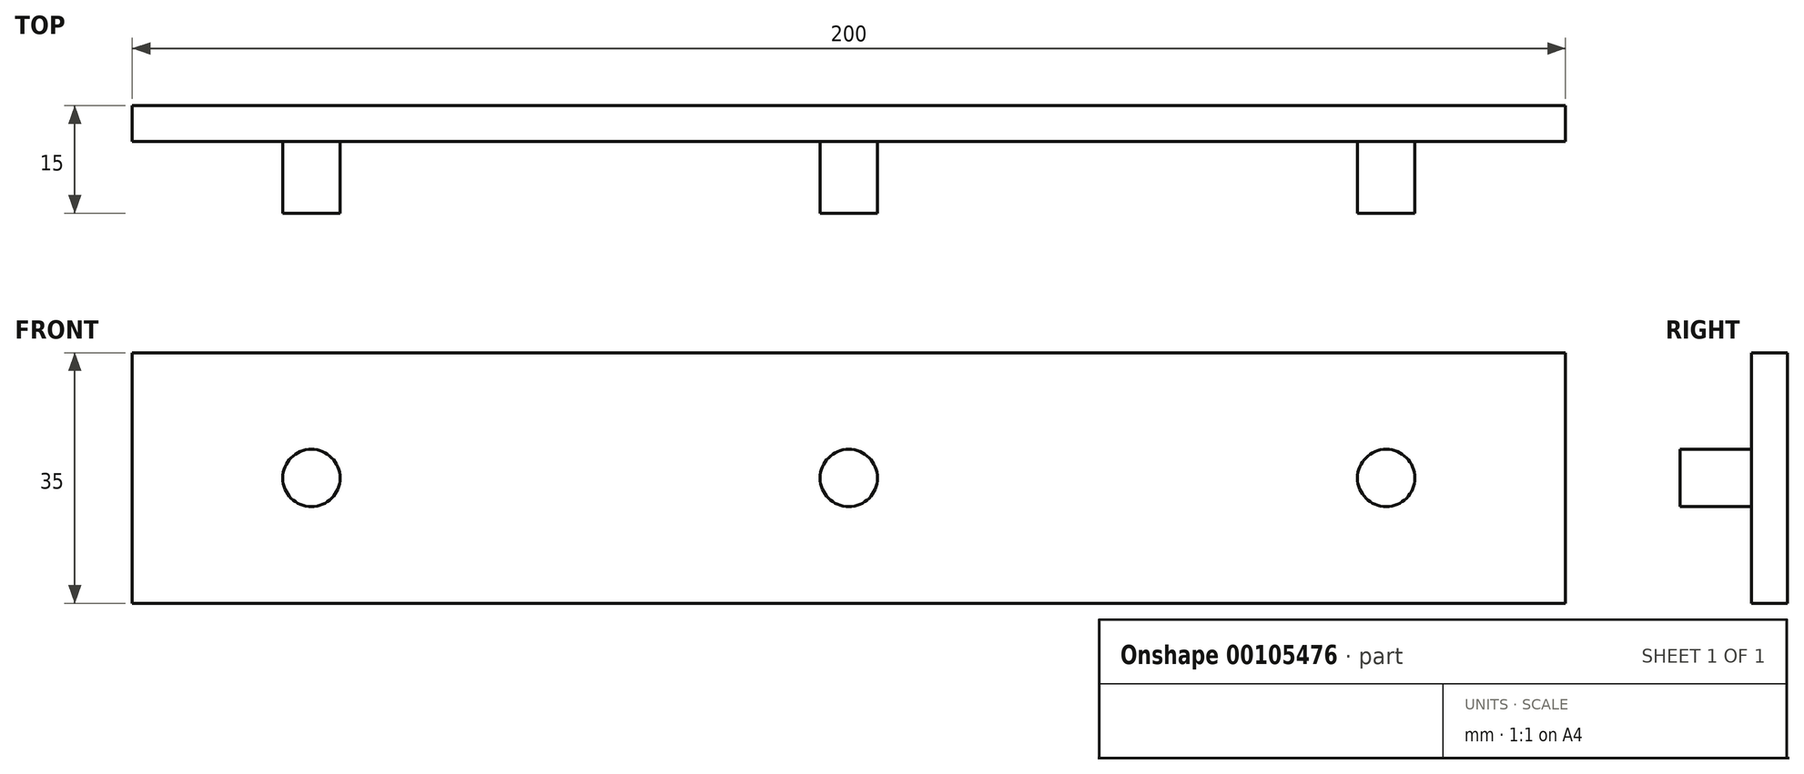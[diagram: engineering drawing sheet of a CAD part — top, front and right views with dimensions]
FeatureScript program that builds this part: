
annotation { "Feature Type Name" : "Feature", "Feature Type Description" : "" }
export const myFeature = defineFeature(function(context is Context, id is Id, definition is map)
    precondition{}
    {
        {
            var Q0;
            Q0=qCreatedBy(makeId("Front.planeOp"),FACE);
            var sketch = newSketch(context, id + "F0", { "sketchPlane" : qUnion([Q0])});
            skLineSegment(sketch, "E0.bottom", {"start": v(100, -17.5) * mm, "end": v(-100, -17.5) * mm});
            skLineSegment(sketch, "E0.top", {"start": v(100, 17.5) * mm, "end": v(-100, 17.5) * mm});
            skLineSegment(sketch, "E0.left", {"start": v(100, -17.5) * mm, "end": v(100, 17.5) * mm});
            skLineSegment(sketch, "E0.right", {"start": v(-100, -17.5) * mm, "end": v(-100, 17.5) * mm});
            skPoint(sketch, "E0.middle", {"position": v(0, 0) * mm});
            skPoint(sketch, "E1.endSnap0", {"position": v(100, 0) * mm});
            skSolve(sketch);
        }
        {
            var Q0;
            Q0=makeQuery(id+"F0.imprint","IMPRINT",FACE,{"disambiguationData":[TD([[makeQuery(id+"F0.imprint","IMPRINT",EDGE,{"derivedFrom":sQuery(id+"F0.wireOp",EDGE,"E0.bottom")}),-1.0]])]});
            extrude(context, id + "F1", {"entities" : qUnion([Q0]), "depth" : 5 * mm});
        }
        {
            var Q0;
            Q0=makeQuery(id+"F1.opExtrude","CAP_FACE",FACE,{"disambiguationData":[OSD([sQuery(id+"F0.wireOp",EDGE,"E0.bottom"),sQuery(id+"F0.wireOp",EDGE,"E0.top"),sQuery(id+"F0.wireOp",EDGE,"E0.left"),sQuery(id+"F0.wireOp",EDGE,"E0.right"),sQuery(id+"F0.wireOp",EDGE,"MOLCSVGj-iSIn-FVQK-9bUl-KHfmUCAzGl1P"),sQuery(id+"F0.wireOp",EDGE,"bs5qCy47-dbud-rpmF-XK5Y-o9ODh18vaSlH"),sQuery(id+"F0.wireOp",EDGE,"29d899b3-f74e-4a81-94b4-cb863c27e3bd0.MirrorC")])],"isStart":false});
            var sketch = newSketch(context, id + "F2", { "sketchPlane" : qUnion([Q0])});
            skCircle(sketch, "E2", {"center": v(-75, 0) * mm, "radius": 4 * mm});
            skCircle(sketch, "E3", {"center": v(0, 0) * mm, "radius": 4 * mm});
            skCircle(sketch, "E4", {"center": v(75, 0) * mm, "radius": 4 * mm});
            skSolve(sketch);
        }
        {
            var Q0;
            Q0 = qSketchRegion(id + "F2", true);
            extrude(context, id + "F3", {"entities" : qUnion([Q0]), "operationType" : NewBodyOperationType.ADD, "depth" : 10 * mm});
        }
    });
